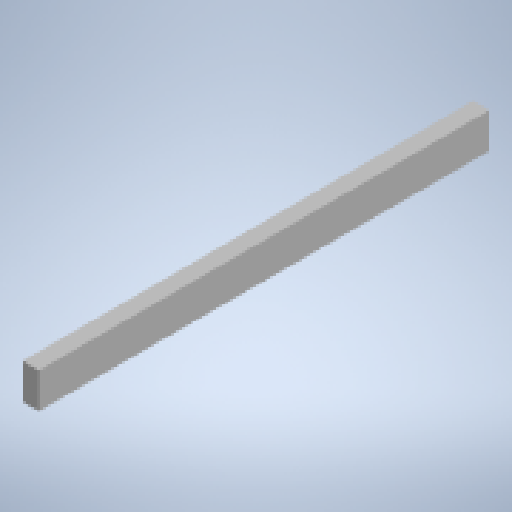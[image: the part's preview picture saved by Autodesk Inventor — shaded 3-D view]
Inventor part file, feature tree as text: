
AUTODESK INVENTOR PART (.ipt)
format: ipt  version: 2023 (Build 270158000, 158)  size: 129,024 bytes
history: native  units: in
note: dims shown in document units (in); Inventor stores cm internally (conversion verified against a paired STEP export)
features: extrude x1, sketch x1
ambient origin geometry x8: Origin, YZ Plane, XZ Plane, XY Plane, X Axis, Y Axis, Z Axis, Center Point
bodies: Solid1 (feature_tree)
feature tree (2):
  extrude  "Extrusion1"  Depth=3.75in
  sketch  "Sketch1"  dims[d0=1.75in d1=3.75in d2=48.0in d3=0.0in]
